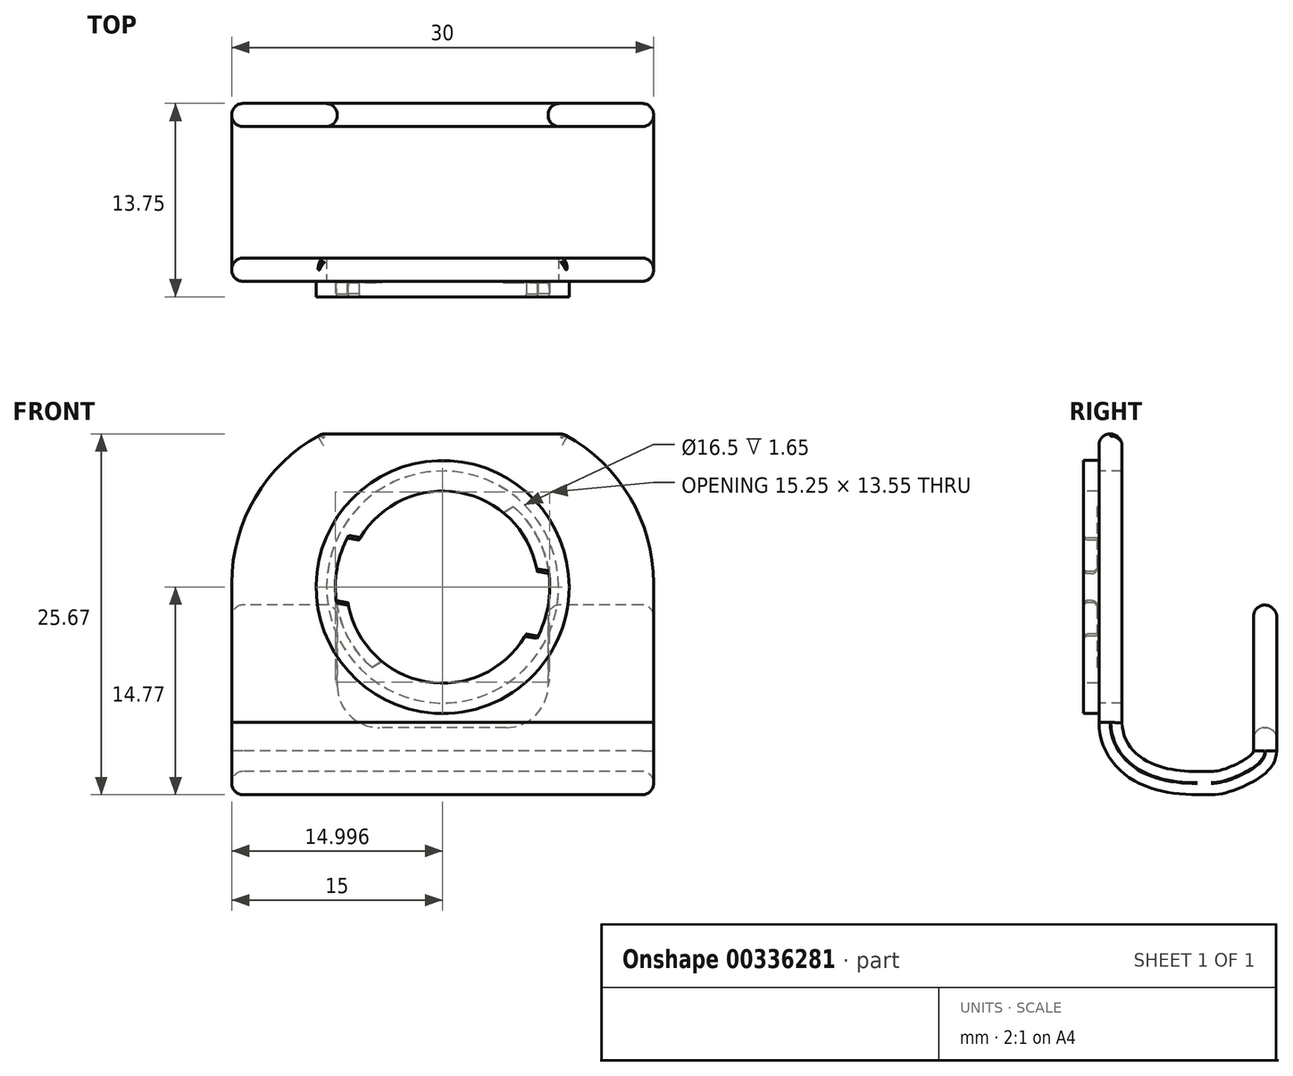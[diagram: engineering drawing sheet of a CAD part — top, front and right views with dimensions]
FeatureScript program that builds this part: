
annotation { "Feature Type Name" : "Feature", "Feature Type Description" : "" }
export const myFeature = defineFeature(function(context is Context, id is Id, definition is map)
    precondition{}
    {
        {
            var Q0;
            Q0=qCreatedBy(makeId("Top.planeOp"),FACE);
            var sketch = newSketch(context, id + "F0", { "sketchPlane" : qUnion([Q0])});
            skArc(sketch, "E0", {"start": v(-2.25, -7.29) * mm, "mid": v(0, -7.62) * mm, "end": v(2.25, -7.29) * mm});
            skArc(sketch, "E1", {"start": v(-2.25, 6.44) * mm, "mid": v(-6.83, 0) * mm, "end": v(-2.25, -6.44) * mm});
            skLineSegment(sketch, "E2", {"start": v(0, -16.23) * mm, "end": v(0, 16.23) * mm, "construction": true});
            skLineSegment(sketch, "E3", {"start": v(2.25, -6.44) * mm, "end": v(-2.25, 6.44) * mm, "construction": true});
            skLineSegment(sketch, "E4", {"start": v(-2.25, -6.44) * mm, "end": v(2.25, 6.44) * mm, "construction": true});
            skPoint(sketch, "E5", {"position": v(-2.25, 6.44) * mm});
            skPoint(sketch, "E6", {"position": v(2.25, 6.44) * mm});
            skPoint(sketch, "E7", {"position": v(2.25, -6.44) * mm});
            skPoint(sketch, "E8", {"position": v(-2.25, -6.44) * mm});
            skLineSegment(sketch, "E9", {"start": v(-2.25, 6.44) * mm, "end": v(-2.25, 7.29) * mm});
            skLineSegment(sketch, "E10", {"start": v(2.25, 6.44) * mm, "end": v(2.25, 7.29) * mm});
            skLineSegment(sketch, "E11", {"start": v(-2.25, -6.44) * mm, "end": v(-2.25, -7.29) * mm});
            skLineSegment(sketch, "E12", {"start": v(2.25, -6.44) * mm, "end": v(2.25, -7.29) * mm});
            skArc(sketch, "E13.trimOffspring", {"start": v(2.25, 7.29) * mm, "mid": v(0, 7.63) * mm, "end": v(-2.25, 7.29) * mm});
            skArc(sketch, "E14.trimOffspring", {"start": v(2.25, -6.44) * mm, "mid": v(6.83, 0) * mm, "end": v(2.25, 6.44) * mm});
            skCircle(sketch, "E15", {"center": v(0, 0) * mm, "radius": 9 * mm});
            skSolve(sketch);
        }
        {
            var Q0;
            Q0 = qSketchRegion(id + "F0", true);
            extrude(context, id + "F1", {"entities" : qUnion([Q0]), "depth" : 1 * mm});
        }
        {
            var Q0;
            Q0=makeQuery(id+"F1.opExtrude","CAP_FACE",FACE,{"disambiguationData":[OSD([sQuery(id+"F0.wireOp",EDGE,"E0"),sQuery(id+"F0.wireOp",EDGE,"E1"),sQuery(id+"F0.wireOp",EDGE,"E9"),sQuery(id+"F0.wireOp",EDGE,"E10"),sQuery(id+"F0.wireOp",EDGE,"E11"),sQuery(id+"F0.wireOp",EDGE,"E12"),sQuery(id+"F0.wireOp",EDGE,"E13.trimOffspring"),sQuery(id+"F0.wireOp",EDGE,"E14.trimOffspring"),sQuery(id+"F0.wireOp",EDGE,"E15")])],"isStart":false});
            var sketch = newSketch(context, id + "F2", { "sketchPlane" : qUnion([Q0])});
            skArc(sketch, "E16", {"start": v(6.51, 3.97) * mm, "mid": v(2.7, 7.13) * mm, "end": v(-2.25, 7.29) * mm});
            skCircle(sketch, "E17", {"center": v(0, 0) * mm, "radius": 9 * mm});
            skArc(sketch, "E18", {"start": v(-2.25, 6.44) * mm, "mid": v(-6.38, 2.42) * mm, "end": v(-5.95, -3.33) * mm});
            skLineSegment(sketch, "E19", {"start": v(-2.25, 6.44) * mm, "end": v(-2.25, 7.29) * mm});
            skLineSegment(sketch, "E20", {"start": v(2.25, -6.44) * mm, "end": v(2.25, -7.29) * mm});
            skLineSegment(sketch, "E21", {"start": v(8.87, 4.97) * mm, "end": v(-9.63, -5.4) * mm, "construction": true});
            skLineSegment(sketch, "E22", {"start": v(3.76, -10.76) * mm, "end": v(-3.88, 11.1) * mm, "construction": true});
            skLineSegment(sketch, "E23", {"start": v(-5.95, -3.33) * mm, "end": v(-6.51, -3.97) * mm});
            skArc(sketch, "E24.trimOffspring", {"start": v(2.25, -6.44) * mm, "mid": v(6.38, -2.42) * mm, "end": v(5.95, 3.33) * mm});
            skArc(sketch, "E25.trimOffspring", {"start": v(-6.51, -3.97) * mm, "mid": v(-2.7, -7.13) * mm, "end": v(2.25, -7.29) * mm});
            skLineSegment(sketch, "E26", {"start": v(5.95, 3.33) * mm, "end": v(6.51, 3.97) * mm});
            skSolve(sketch);
        }
        {
            var Q0;
            Q0 = qSketchRegion(id + "F2", true);
            extrude(context, id + "F3", {"entities" : qUnion([Q0]), "operationType" : NewBodyOperationType.ADD, "depth" : 1.75 * mm});
        }
        {
            var Q0;
            Q0=makeQuery(id+"F1.opExtrude","CAP_EDGE",EDGE,{"disambiguationData":[OSD([sQuery(id+"F0.wireOp",EDGE,"E10")])],"isStart":false});
            var Q1;
            Q1=makeQuery(id+"F1.opExtrude","CAP_EDGE",EDGE,{"disambiguationData":[OSD([sQuery(id+"F0.wireOp",EDGE,"E11")])],"isStart":false});
            fillet(context, id + "F4", {"entities" : qUnion([Q0, Q1]), "radius" : 0.4 * mm, "tangentPropagation" : true, "allowEdgeOverflow" : false});
        }
        {
            var Q0;
            Q0=makeQuery(id+"F1.opExtrude","CAP_EDGE",EDGE,{"disambiguationData":[OSD([sQuery(id+"F0.wireOp",EDGE,"E12")])],"isStart":true});
            var Q1;
            Q1=makeQuery(id+"F1.opExtrude","CAP_EDGE",EDGE,{"disambiguationData":[OSD([sQuery(id+"F0.wireOp",EDGE,"E11")])],"isStart":true});
            var Q2;
            Q2=makeQuery(id+"F1.opExtrude","CAP_EDGE",EDGE,{"disambiguationData":[OSD([sQuery(id+"F0.wireOp",EDGE,"E10")])],"isStart":true});
            var Q3;
            Q3=makeQuery(id+"F1.opExtrude","CAP_EDGE",EDGE,{"disambiguationData":[OSD([sQuery(id+"F0.wireOp",EDGE,"E9")])],"isStart":true});
            chamfer(context, id + "F5", {"entities" : qUnion([Q0, Q1, Q2, Q3]), "width" : 0.2 * mm, "tangentPropagation" : true});
        }
        {
            var Q0;
            Q0=qCreatedBy(makeId("Right.planeOp"),FACE);
            var sketch = newSketch(context, id + "F6", { "sketchPlane" : qUnion([Q0])});
            skLineSegment(sketch, "E27.bottom", {"start": v(0, 12.1) * mm, "end": v(11.66, 12.1) * mm});
            skLineSegment(sketch, "E27.top", {"start": v(-10.35, 2.75) * mm, "end": v(9.65, 2.75) * mm});
            skLineSegment(sketch, "E27.right", {"start": v(13.12, 9.1) * mm, "end": v(13.12, 8.1) * mm});
            skFitSpline(sketch, "E28", {"points": [v(13.12, 9.1) * mm, v(11.66, 12.1) * mm], "startDerivative": vector(0, 3.05) * mm, "endDerivative": vector(-1.2, -0.05) * mm});
            skFitSpline(sketch, "E29", {"points": [v(9.65, 2.75) * mm, v(13.12, 8.1) * mm], "startDerivative": vector(0.5, -0.03) * mm, "endDerivative": vector(0, 16.27) * mm});
            skLineSegment(sketch, "E30", {"start": v(0, 12.1) * mm, "end": v(-10.35, 2.75) * mm});
            skLineSegment(sketch, "E31", {"start": v(0, -1.58) * mm, "end": v(0, 15.23) * mm, "construction": true});
            skSolve(sketch);
        }
        {
            var Q0;
            Q0=makeQuery(id+"F6.imprint","IMPRINT",FACE,{"disambiguationData":[TD([[makeQuery(id+"F6.imprint","IMPRINT",EDGE,{"derivedFrom":sQuery(id+"F6.wireOp",EDGE,"E27.right")}),-1.0]])]});
            extrude(context, id + "F7", {"entities" : qUnion([Q0]), "endBound" : BoundingType.SYMMETRIC, "depth" : 30 * mm});
        }
        {
            var Q0;
            Q0=makeQuery(id+"F7.opExtrude","CAP_FACE",FACE,{"disambiguationData":[OSD([sQuery(id+"F6.wireOp",EDGE,"E27.right"),sQuery(id+"F6.wireOp",EDGE,"E27.bottom"),sQuery(id+"F6.wireOp",EDGE,"E27.top"),sQuery(id+"F6.wireOp",EDGE,"E28"),sQuery(id+"F6.wireOp",EDGE,"E29"),sQuery(id+"F6.wireOp",EDGE,"E30")])],"isStart":false});
            var Q1;
            Q1=makeQuery(id+"F7.opExtrude","SWEPT_FACE",FACE,{"disambiguationData":[OSD([sQuery(id+"F6.wireOp",EDGE,"E30")])]});
            var Q2;
            Q2=makeQuery(id+"F7.opExtrude","CAP_FACE",FACE,{"disambiguationData":[OSD([sQuery(id+"F6.wireOp",EDGE,"E27.right"),sQuery(id+"F6.wireOp",EDGE,"E27.bottom"),sQuery(id+"F6.wireOp",EDGE,"E27.top"),sQuery(id+"F6.wireOp",EDGE,"E28"),sQuery(id+"F6.wireOp",EDGE,"E29"),sQuery(id+"F6.wireOp",EDGE,"E30")])],"isStart":true});
            shell(context, id + "F8", {"entities" : qUnion([Q0, Q1, Q2]), "thickness" : 1.65 * mm, "oppositeDirection" : true});
        }
        {
            var Q0;
            Q0=makeQuery(id+"F7.opExtrude","SWEPT_FACE",FACE,{"disambiguationData":[OSD([sQuery(id+"F6.wireOp",EDGE,"E27.top")])]});
            var sketch = newSketch(context, id + "F9", { "sketchPlane" : qUnion([Q0])});
            skCircle(sketch, "E32", {"center": v(0, 0) * mm, "radius": 8.25 * mm});
            skSolve(sketch);
        }
        {
            var Q0;
            Q0=makeQuery(id+"F9.imprint","IMPRINT",FACE,{"disambiguationData":[TD([[makeQuery(id+"F9.imprint","IMPRINT",EDGE,{"derivedFrom":sQuery(id+"F9.wireOp",EDGE,"E32")}),1.0]])]});
            var Q1;
            Q1=makeQuery(id+"F8.opShell","OFFSET_FACE",FACE,{"disambiguationData":[OSD([sQuery(id+"F6.wireOp",EDGE,"E27.top")])]});
            extrude(context, id + "F10", {"entities" : qUnion([Q0]), "operationType" : NewBodyOperationType.REMOVE, "endBound" : BoundingType.UP_TO_SURFACE, "oppositeDirection" : true, "endBoundEntityFace" : qUnion([Q1]), "depth" : 25 * mm});
        }
        {
            var Q0;
            Q0=qCreatedBy(makeId("Front.planeOp"),FACE);
            var sketch = newSketch(context, id + "F11", { "sketchPlane" : qUnion([Q0])});
            skLineSegment(sketch, "E33", {"start": v(0, -35.62) * mm, "end": v(0, 54.81) * mm, "construction": true});
            skSolve(sketch);
        }
        {
            var Q0;
            Q0=makeQuery(id+"F1.opExtrude","SWEPT_BODY",BODY,{"disambiguationData":[OSD([sQuery(id+"F0.wireOp",EDGE,"E0"),sQuery(id+"F0.wireOp",EDGE,"E1"),sQuery(id+"F0.wireOp",EDGE,"E9"),sQuery(id+"F0.wireOp",EDGE,"E10"),sQuery(id+"F0.wireOp",EDGE,"E11"),sQuery(id+"F0.wireOp",EDGE,"E12"),sQuery(id+"F0.wireOp",EDGE,"E13.trimOffspring"),sQuery(id+"F0.wireOp",EDGE,"E14.trimOffspring"),sQuery(id+"F0.wireOp",EDGE,"E15")])]});
            var Q1;
            Q1=sQuery(id+"F11.wireOp",EDGE,"E33");
            transform(context, id + "F12", {"entities" : qUnion([Q0]), "transformType" : TransformType.ROTATION, "transformAxis" : qUnion([Q1]), "angle" : 100 * degree, "makeCopy" : false});
        }
        {
            var Q0;
            Q0=makeQuery(id+"F7.opExtrude","SWEPT_BODY",BODY,{"disambiguationData":[OSD([sQuery(id+"F6.wireOp",EDGE,"E27.left"),sQuery(id+"F6.wireOp",EDGE,"E27.right"),sQuery(id+"F6.wireOp",EDGE,"E27.bottom"),sQuery(id+"F6.wireOp",EDGE,"E27.top"),sQuery(id+"F6.wireOp",EDGE,"E28"),sQuery(id+"F6.wireOp",EDGE,"E29")])]});
            var Q1;
            Q1=makeQuery(id+"F1.opExtrude","SWEPT_BODY",BODY,{"disambiguationData":[OSD([sQuery(id+"F0.wireOp",EDGE,"E0"),sQuery(id+"F0.wireOp",EDGE,"E1"),sQuery(id+"F0.wireOp",EDGE,"E9"),sQuery(id+"F0.wireOp",EDGE,"E10"),sQuery(id+"F0.wireOp",EDGE,"E11"),sQuery(id+"F0.wireOp",EDGE,"E12"),sQuery(id+"F0.wireOp",EDGE,"E13.trimOffspring"),sQuery(id+"F0.wireOp",EDGE,"E14.trimOffspring"),sQuery(id+"F0.wireOp",EDGE,"E15")])]});
            booleanBodies(context, id + "F13", {"operationType" : BooleanOperationType.UNION, "tools" : qUnion([Q0, Q1])});
        }
        {
            var Q0;
            Q0=makeQuery(id+"F7.opExtrude","SWEPT_FACE",FACE,{"disambiguationData":[OSD([sQuery(id+"F6.wireOp",EDGE,"E27.bottom")])]});
            var sketch = newSketch(context, id + "F14", { "sketchPlane" : qUnion([Q0])});
            skLineSegment(sketch, "E34", {"start": v(0, -11.05) * mm, "end": v(0, 9.42) * mm, "construction": true});
            skLineSegment(sketch, "E35.bottom", {"start": v(-4.5, 10) * mm, "end": v(4.5, 10) * mm});
            skLineSegment(sketch, "E35.top", {"start": v(-7.5, 0) * mm, "end": v(7.5, 0) * mm});
            skLineSegment(sketch, "E35.left", {"start": v(-7.5, 7) * mm, "end": v(-7.5, 0) * mm});
            skLineSegment(sketch, "E35.right", {"start": v(7.5, 7) * mm, "end": v(7.5, 0) * mm});
            skPoint(sketch, "E36.visualSharp", {"position": v(-7.5, 10) * mm});
            skArc(sketch, "E36.filletArc", {"start": v(-4.5, 10) * mm, "mid": v(-6.62, 9.12) * mm, "end": v(-7.5, 7) * mm});
            skPoint(sketch, "E37.visualSharp", {"position": v(7.5, 10) * mm});
            skArc(sketch, "E37.filletArc", {"start": v(7.5, 7) * mm, "mid": v(6.62, 9.12) * mm, "end": v(4.5, 10) * mm});
            skSolve(sketch);
        }
        {
            var Q0;
            Q0 = qSketchRegion(id + "F14", true);
            var Q1;
            Q1=makeQuery(id+"F8.opShell","OFFSET_FACE",FACE,{"disambiguationData":[OSD([sQuery(id+"F6.wireOp",EDGE,"E27.bottom")])]});
            extrude(context, id + "F15", {"entities" : qUnion([Q0]), "operationType" : NewBodyOperationType.REMOVE, "endBound" : BoundingType.UP_TO_SURFACE, "oppositeDirection" : true, "endBoundEntityFace" : qUnion([Q1]), "depth" : 25 * mm});
        }
        {
            var Q0;
            Q0=makeQuery(id+"F7.opExtrude","SWEPT_FACE",FACE,{"disambiguationData":[OSD([sQuery(id+"F6.wireOp",EDGE,"E27.top")])]});
            var sketch = newSketch(context, id + "F16", { "sketchPlane" : qUnion([Q0])});
            skPoint(sketch, "E38.visualSharp", {"position": v(-15, 12.18) * mm});
            skArc(sketch, "E38.filletArc", {"start": v(-1.58, 12.18) * mm, "mid": v(-10.97, 9.24) * mm, "end": v(-15, 0.27) * mm});
            skPoint(sketch, "E39.visualSharp", {"position": v(19, 12.18) * mm});
            skLineSegment(sketch, "E40", {"start": v(-15, 0.27) * mm, "end": v(-15, 12.18) * mm});
            skLineSegment(sketch, "E41", {"start": v(-15, 12.18) * mm, "end": v(-1.58, 12.18) * mm});
            skLineSegment(sketch, "E42", {"start": v(0, -1.72) * mm, "end": v(0, 15.08) * mm, "construction": true});
            skPoint(sketch, "E42.endSnap0", {"position": v(0, 12.18) * mm});
            skArc(sketch, "E43.MirrorCS", {"start": v(1.58, 12.18) * mm, "mid": v(10.97, 9.24) * mm, "end": v(15, 0.27) * mm});
            skLineSegment(sketch, "E44.MirrorCS", {"start": v(15, 12.18) * mm, "end": v(1.58, 12.18) * mm});
            skLineSegment(sketch, "E45.MirrorCS", {"start": v(15, 0.27) * mm, "end": v(15, 12.18) * mm});
            skSolve(sketch);
        }
        {
            var Q0;
            Q0 = qSketchRegion(id + "F16", true);
            var Q1;
            Q1=makeQuery(id+"F13.opBoolean","MERGE",FACE,{"derivedFrom":[makeQuery(id+"F3.opExtrude","CAP_FACE",FACE,{"disambiguationData":[OSD([sQuery(id+"F2.wireOp",EDGE,"E16"),sQuery(id+"F2.wireOp",EDGE,"E17"),sQuery(id+"F2.wireOp",EDGE,"E18"),sQuery(id+"F2.wireOp",EDGE,"E19"),sQuery(id+"F2.wireOp",EDGE,"E20"),sQuery(id+"F2.wireOp",EDGE,"E23"),sQuery(id+"F2.wireOp",EDGE,"E24.trimOffspring"),sQuery(id+"F2.wireOp",EDGE,"E25.trimOffspring"),sQuery(id+"F2.wireOp",EDGE,"E26")])],"isStart":false}),makeQuery(id+"F8.opShell","OFFSET_FACE",FACE,{"disambiguationData":[OSD([sQuery(id+"F6.wireOp",EDGE,"E27.top")])]})]});
            extrude(context, id + "F17", {"entities" : qUnion([Q0]), "operationType" : NewBodyOperationType.REMOVE, "endBound" : BoundingType.UP_TO_SURFACE, "oppositeDirection" : true, "endBoundEntityFace" : qUnion([Q1]), "depth" : 25 * mm});
        }
        {
            var Q0;
            Q0=makeQuery(id+"F7.opExtrude","CAP_FACE",FACE,{"disambiguationData":[OSD([sQuery(id+"F6.wireOp",EDGE,"E27.right"),sQuery(id+"F6.wireOp",EDGE,"E27.bottom"),sQuery(id+"F6.wireOp",EDGE,"E27.top"),sQuery(id+"F6.wireOp",EDGE,"E28"),sQuery(id+"F6.wireOp",EDGE,"E29"),sQuery(id+"F6.wireOp",EDGE,"E30")])],"isStart":false});
            var Q1;
            {var subQ0=sQuery(id+"F6.wireOp",EDGE,"E30");Q1=makeQuery(id+"F15.boolean.opBoolean","SPLIT",FACE,{"disambiguationData":[TD([makeQuery(id+"F15.opExtrude","SWEPT_FACE",FACE,{"disambiguationData":[OSD([sQuery(id+"F14.wireOp",EDGE,"E35.right")])]})])],"derivedFrom":makeQuery(id+"F8.opShell","OFFSET_FACE",FACE,{"disambiguationData":[OSD([subQ0])]})});}
            var Q2;
            {var subQ0=sQuery(id+"F6.wireOp",EDGE,"E30");Q2=makeQuery(id+"F15.boolean.opBoolean","SPLIT",FACE,{"disambiguationData":[TD([makeQuery(id+"F15.opExtrude","SWEPT_FACE",FACE,{"disambiguationData":[OSD([sQuery(id+"F14.wireOp",EDGE,"E35.left")])]})])],"derivedFrom":makeQuery(id+"F8.opShell","OFFSET_FACE",FACE,{"disambiguationData":[OSD([subQ0])]})});}
            var Q3;
            Q3=makeQuery(id+"F15.boolean.opBoolean","COPY",FACE,{"derivedFrom":makeQuery(id+"F15.opExtrude","SWEPT_FACE",FACE,{"disambiguationData":[OSD([sQuery(id+"F14.wireOp",EDGE,"E35.right")])]})});
            var Q4;
            Q4=makeQuery(id+"F7.opExtrude","SWEPT_EDGE",EDGE,{"disambiguationData":[OSD([sQuery(id+"F6.wireOp",EDGE,"E27.top"),sQuery(id+"F6.wireOp",EDGE,"E30")])]});
            var Q5;
            Q5=makeQuery(id+"F7.opExtrude","CAP_FACE",FACE,{"disambiguationData":[OSD([sQuery(id+"F6.wireOp",EDGE,"E27.right"),sQuery(id+"F6.wireOp",EDGE,"E27.bottom"),sQuery(id+"F6.wireOp",EDGE,"E27.top"),sQuery(id+"F6.wireOp",EDGE,"E28"),sQuery(id+"F6.wireOp",EDGE,"E29"),sQuery(id+"F6.wireOp",EDGE,"E30")])],"isStart":true});
            var Q6;
            Q6=makeQuery(id+"F15.boolean.opBoolean","COPY",FACE,{"derivedFrom":makeQuery(id+"F15.opExtrude","SWEPT_FACE",FACE,{"disambiguationData":[OSD([sQuery(id+"F14.wireOp",EDGE,"E35.left")])]})});
            var Q7;
            Q7=makeQuery(id+"F15.boolean.opBoolean","COPY",FACE,{"derivedFrom":makeQuery(id+"F15.opExtrude","SWEPT_FACE",FACE,{"disambiguationData":[OSD([sQuery(id+"F14.wireOp",EDGE,"E36.filletArc")])]})});
            var Q8;
            Q8=makeQuery(id+"F15.boolean.opBoolean","COPY",FACE,{"derivedFrom":makeQuery(id+"F15.opExtrude","SWEPT_FACE",FACE,{"disambiguationData":[OSD([sQuery(id+"F14.wireOp",EDGE,"E35.bottom")])]})});
            var Q9;
            Q9=makeQuery(id+"F15.boolean.opBoolean","COPY",FACE,{"derivedFrom":makeQuery(id+"F15.opExtrude","SWEPT_FACE",FACE,{"disambiguationData":[OSD([sQuery(id+"F14.wireOp",EDGE,"E37.filletArc")])]})});
            var Q10;
            Q10=makeQuery(id+"F7.opExtrude","SWEPT_FACE",FACE,{"disambiguationData":[OSD([sQuery(id+"F6.wireOp",EDGE,"E30")])]});
            fillet(context, id + "F18", {"entities" : qUnion([Q0, Q1, Q2, Q3, Q4, Q5, Q6, Q7, Q8, Q9, Q10]), "radius" : 0.8 * mm, "tangentPropagation" : true, "allowEdgeOverflow" : false});
        }
        {
            var Q0;
            Q0=makeQuery(id+"F7.opExtrude","SWEPT_BODY",BODY,{"disambiguationData":[OSD([sQuery(id+"F6.wireOp",EDGE,"E27.right"),sQuery(id+"F6.wireOp",EDGE,"E27.bottom"),sQuery(id+"F6.wireOp",EDGE,"E27.top"),sQuery(id+"F6.wireOp",EDGE,"E28"),sQuery(id+"F6.wireOp",EDGE,"E29"),sQuery(id+"F6.wireOp",EDGE,"E30")])]});
            var Q1;
            Q1=makeQuery(id+"F7.opExtrude","SWEPT_EDGE",EDGE,{"disambiguationData":[OSD([sQuery(id+"F6.wireOp",EDGE,"E27.right"),sQuery(id+"F6.wireOp",EDGE,"E29")])]});
            transform(context, id + "F19", {"entities" : qUnion([Q0]), "transformType" : TransformType.ROTATION, "transformAxis" : qUnion([Q1]), "angle" : 90 * degree, "oppositeDirection" : true, "makeCopy" : false});
        }
    });
